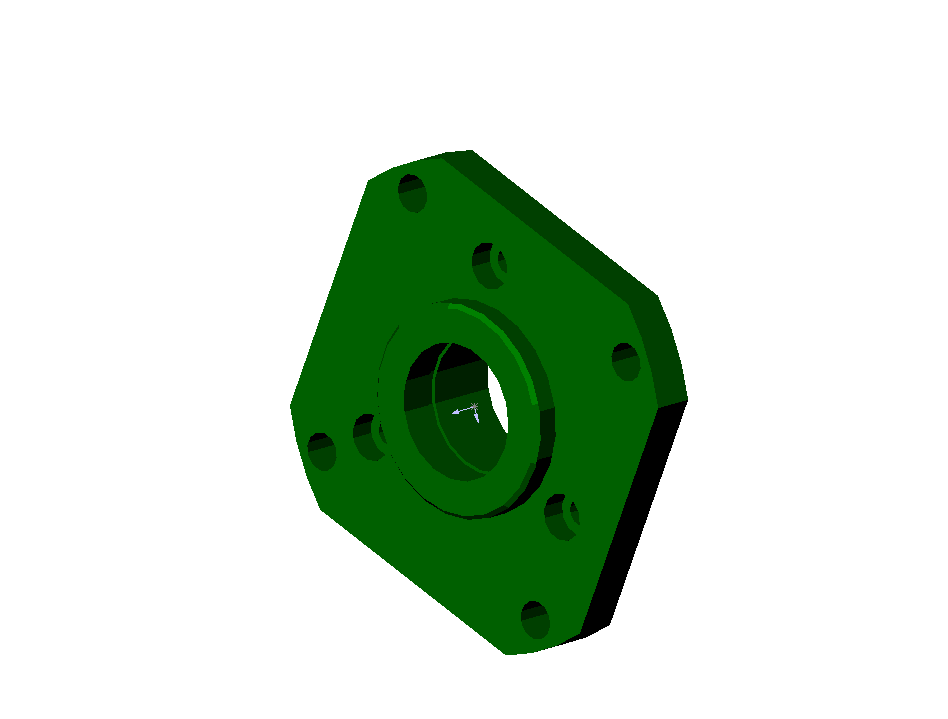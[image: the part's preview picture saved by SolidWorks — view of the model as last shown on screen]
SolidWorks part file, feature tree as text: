
SOLIDWORKS PART (.sldprt)
format: sldprt  version: not decoded by parser v0  size: 155,136 bytes
history: native  units: mm
features: sketch x9, cut_extrude x6, plane x4, extrude x3, pattern_circular x3, material x1, chamfer x1 (+10 scaffold rows collapsed)
feature tree (37):
  scaffold x10  (default folders/planes/origin — collapsed)
  material  "Matériau <non spécifié>"
  plane  "Plan1"
  plane  "Plan2"
  plane  "Plan3"
  sketch  "Esquisse1"  dims[D1=57.0mm]
  extrude  "Base-Extrusion"  Depth=5mm
  sketch  "Esquisse2"  dims[D1=30.0mm]
  extrude  "Boss.-Extru.1"  Depth=6mm
  sketch  "Esquisse3"  dims[D1=25.0mm]
  extrude  "Boss.-Extru.2"  Depth=3mm
  chamfer  "Chanfrein1"  Distance=0.5mm Angle=45deg
  sketch  "Esquisse4"  dims[D1=16.0mm]
  cut_extrude  "Enlèv. mat.-Extru.1"  [1 undecoded]
  sketch  "Esquisse5"  dims[D2=4.5mm D1=25.0mm]
  cut_extrude  "Enlèv. mat.-Extru.2"  [1 undecoded]
  pattern_circular  "Répétition circulaire1"  Count=4 Angle=90deg
  sketch  "Esquisse6"  dims[D2=5.5mm D1=17.0mm]
  cut_extrude  "Enlèv. mat.-Extru.4"  Depth=3mm
  sketch  "Esquisse8"  dims[D1=3.0mm]
  cut_extrude  "Enlèv. mat.-Extru.5"  [1 undecoded]
  pattern_circular  "Répétition circulaire2"  Count=3 Angle=120deg
  plane  "Plan4"  Offset=4mm
  sketch  "Esquisse9"  dims[D1=16.8mm]
  cut_extrude  "Enlèv. mat.-Extru.6"  Depth=1.1mm
  sketch  "Esquisse10"  dims[D1=24.0mm]
  cut_extrude  "Enlèv. mat.-Extru.7"  [1 undecoded]
  pattern_circular  "Répétition circulaire3"  Count=4 Angle=90deg
decode coverage: 18 of 22 modeling features carry decoded parameters
note: 4 parameter values undecoded
summary: no parameter record found for 4 features
note: suppression state not decoded; provenance and decode notes live in map.json
